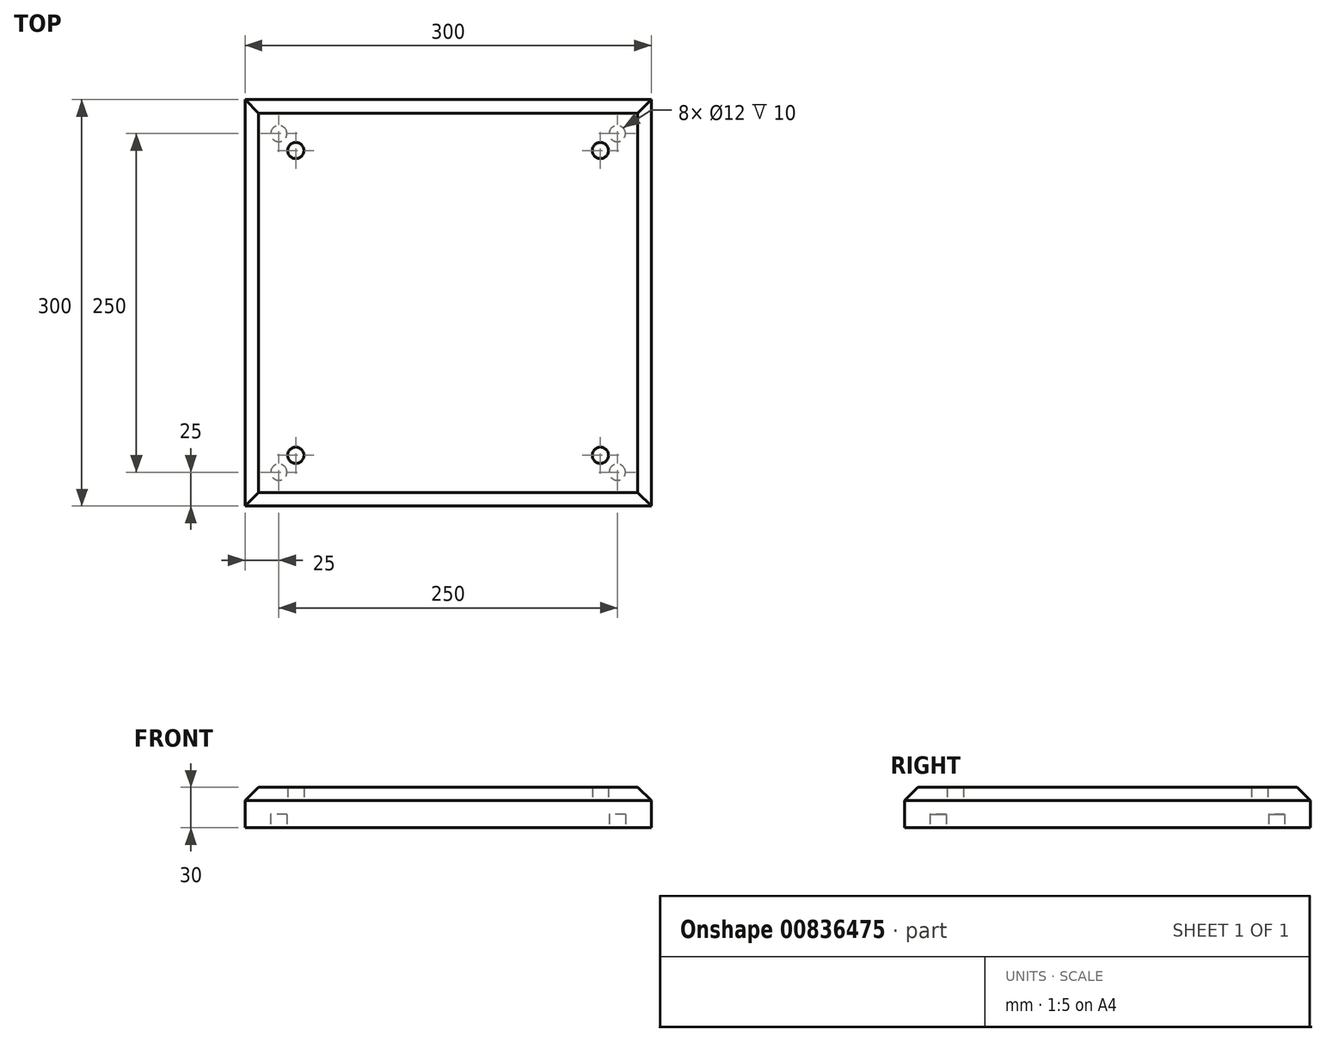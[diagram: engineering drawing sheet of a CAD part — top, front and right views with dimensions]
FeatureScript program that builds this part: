
annotation { "Feature Type Name" : "Feature", "Feature Type Description" : "" }
export const myFeature = defineFeature(function(context is Context, id is Id, definition is map)
    precondition{}
    {
        {
            var Q0;
            Q0=qCreatedBy(makeId("Top.planeOp"),FACE);
            var sketch = newSketch(context, id + "F0", { "sketchPlane" : qUnion([Q0])});
            skLineSegment(sketch, "E0.0", {"start": v(150, 150) * mm, "end": v(150, -150) * mm});
            skLineSegment(sketch, "E0.1", {"start": v(150, -150) * mm, "end": v(-150, -150) * mm});
            skLineSegment(sketch, "E0.2", {"start": v(-150, -150) * mm, "end": v(-150, 150) * mm});
            skLineSegment(sketch, "E0.3", {"start": v(-150, 150) * mm, "end": v(150, 150) * mm});
            skPoint(sketch, "E0.0.midPoint", {"position": v(150, 0) * mm});
            skLineSegment(sketch, "E1.0", {"start": v(112.5, 112.5) * mm, "end": v(112.5, -112.5) * mm, "construction": true});
            skLineSegment(sketch, "E1.1", {"start": v(112.5, -112.5) * mm, "end": v(-112.5, -112.5) * mm, "construction": true});
            skLineSegment(sketch, "E1.2", {"start": v(-112.5, -112.5) * mm, "end": v(-112.5, 112.5) * mm, "construction": true});
            skLineSegment(sketch, "E1.3", {"start": v(-112.5, 112.5) * mm, "end": v(112.5, 112.5) * mm, "construction": true});
            skPoint(sketch, "E1.0.midPoint", {"position": v(112.5, 0) * mm});
            skCircle(sketch, "E2", {"center": v(-112.5, -112.5) * mm, "radius": 6 * mm});
            skCircle(sketch, "E3", {"center": v(112.5, -112.5) * mm, "radius": 6 * mm});
            skCircle(sketch, "E4", {"center": v(112.5, 112.5) * mm, "radius": 6 * mm});
            skCircle(sketch, "E5", {"center": v(-112.5, 112.5) * mm, "radius": 6 * mm});
            skLineSegment(sketch, "E6.0", {"start": v(125, 125) * mm, "end": v(125, -125) * mm, "construction": true});
            skLineSegment(sketch, "E6.1", {"start": v(125, -125) * mm, "end": v(-125, -125) * mm, "construction": true});
            skLineSegment(sketch, "E6.2", {"start": v(-125, -125) * mm, "end": v(-125, 125) * mm, "construction": true});
            skLineSegment(sketch, "E6.3", {"start": v(-125, 125) * mm, "end": v(125, 125) * mm, "construction": true});
            skPoint(sketch, "E6.0.midPoint", {"position": v(125, 0) * mm});
            skCircle(sketch, "E7", {"center": v(-125, -125) * mm, "radius": 6 * mm});
            skCircle(sketch, "E8", {"center": v(-125, 125) * mm, "radius": 6 * mm});
            skCircle(sketch, "E9", {"center": v(125, 125) * mm, "radius": 6 * mm});
            skCircle(sketch, "E10", {"center": v(125, -125) * mm, "radius": 6 * mm});
            skSolve(sketch);
        }
        {
            var Q0;
            Q0=makeQuery(id+"F0.imprint","IMPRINT",FACE,{"disambiguationData":[TD([[makeQuery(id+"F0.imprint","IMPRINT",EDGE,{"derivedFrom":sQuery(id+"F0.wireOp",EDGE,"E0.0")}),-1.0]])]});
            extrude(context, id + "F1", {"entities" : qUnion([Q0]), "endBound" : BoundingType.SYMMETRIC, "depth" : 30 * mm, "offsetDistance" : 25 * mm});
        }
        {
            var Q0;
            Q0=makeQuery(id+"F1.opExtrude","CAP_EDGE",EDGE,{"disambiguationData":[OSD([sQuery(id+"F0.wireOp",EDGE,"E0.3")])],"isStart":false});
            var Q1;
            Q1=makeQuery(id+"F1.opExtrude","CAP_EDGE",EDGE,{"disambiguationData":[OSD([sQuery(id+"F0.wireOp",EDGE,"E0.1")])],"isStart":false});
            var Q2;
            Q2=makeQuery(id+"F1.opExtrude","CAP_EDGE",EDGE,{"disambiguationData":[OSD([sQuery(id+"F0.wireOp",EDGE,"E0.0")])],"isStart":false});
            var Q3;
            Q3=makeQuery(id+"F1.opExtrude","CAP_EDGE",EDGE,{"disambiguationData":[OSD([sQuery(id+"F0.wireOp",EDGE,"E0.2")])],"isStart":false});
            chamfer(context, id + "F2", {"entities" : qUnion([Q0, Q1, Q2, Q3]), "chamferType" : ChamferType.OFFSET_ANGLE, "width" : 10 * mm, "oppositeDirection" : false, "angle" : 45 * degree, "tangentPropagation" : true});
        }
        {
            var Q0;
            Q0=makeQuery(id+"F0.imprint","IMPRINT",FACE,{"disambiguationData":[TD([[makeQuery(id+"F0.imprint","IMPRINT",EDGE,{"derivedFrom":sQuery(id+"F0.wireOp",EDGE,"E5")}),1.0]])]});
            var Q1;
            Q1=makeQuery(id+"F0.imprint","IMPRINT",FACE,{"disambiguationData":[TD([[makeQuery(id+"F0.imprint","IMPRINT",EDGE,{"derivedFrom":sQuery(id+"F0.wireOp",EDGE,"E4")}),1.0]])]});
            var Q2;
            Q2=makeQuery(id+"F0.imprint","IMPRINT",FACE,{"disambiguationData":[TD([[makeQuery(id+"F0.imprint","IMPRINT",EDGE,{"derivedFrom":sQuery(id+"F0.wireOp",EDGE,"E3")}),1.0]])]});
            var Q3;
            Q3=makeQuery(id+"F0.imprint","IMPRINT",FACE,{"disambiguationData":[TD([[makeQuery(id+"F0.imprint","IMPRINT",EDGE,{"derivedFrom":sQuery(id+"F0.wireOp",EDGE,"E2")}),1.0]])]});
            extrude(context, id + "F3", {"entities" : qUnion([Q0, Q1, Q2, Q3]), "operationType" : NewBodyOperationType.ADD, "depth" : 5 * mm, "offsetDistance" : 25 * mm, "hasSecondDirection" : true, "secondDirectionOppositeDirection" : true, "secondDirectionDepth" : 15 * mm});
        }
        {
            var Q0;
            Q0=makeQuery(id+"F0.imprint","IMPRINT",FACE,{"disambiguationData":[TD([[makeQuery(id+"F0.imprint","IMPRINT",EDGE,{"derivedFrom":sQuery(id+"F0.wireOp",EDGE,"E8")}),1.0]])]});
            var Q1;
            Q1=makeQuery(id+"F0.imprint","IMPRINT",FACE,{"disambiguationData":[TD([[makeQuery(id+"F0.imprint","IMPRINT",EDGE,{"derivedFrom":sQuery(id+"F0.wireOp",EDGE,"E9")}),1.0]])]});
            var Q2;
            Q2=makeQuery(id+"F0.imprint","IMPRINT",FACE,{"disambiguationData":[TD([[makeQuery(id+"F0.imprint","IMPRINT",EDGE,{"derivedFrom":sQuery(id+"F0.wireOp",EDGE,"E10")}),1.0]])]});
            var Q3;
            Q3=makeQuery(id+"F0.imprint","IMPRINT",FACE,{"disambiguationData":[TD([[makeQuery(id+"F0.imprint","IMPRINT",EDGE,{"derivedFrom":sQuery(id+"F0.wireOp",EDGE,"E7")}),1.0]])]});
            extrude(context, id + "F4", {"entities" : qUnion([Q0, Q1, Q2, Q3]), "operationType" : NewBodyOperationType.ADD, "oppositeDirection" : true, "depth" : 5 * mm, "offsetDistance" : 25 * mm, "hasSecondDirection" : true, "secondDirectionOppositeDirection" : false, "secondDirectionDepth" : 15 * mm});
        }
    });
